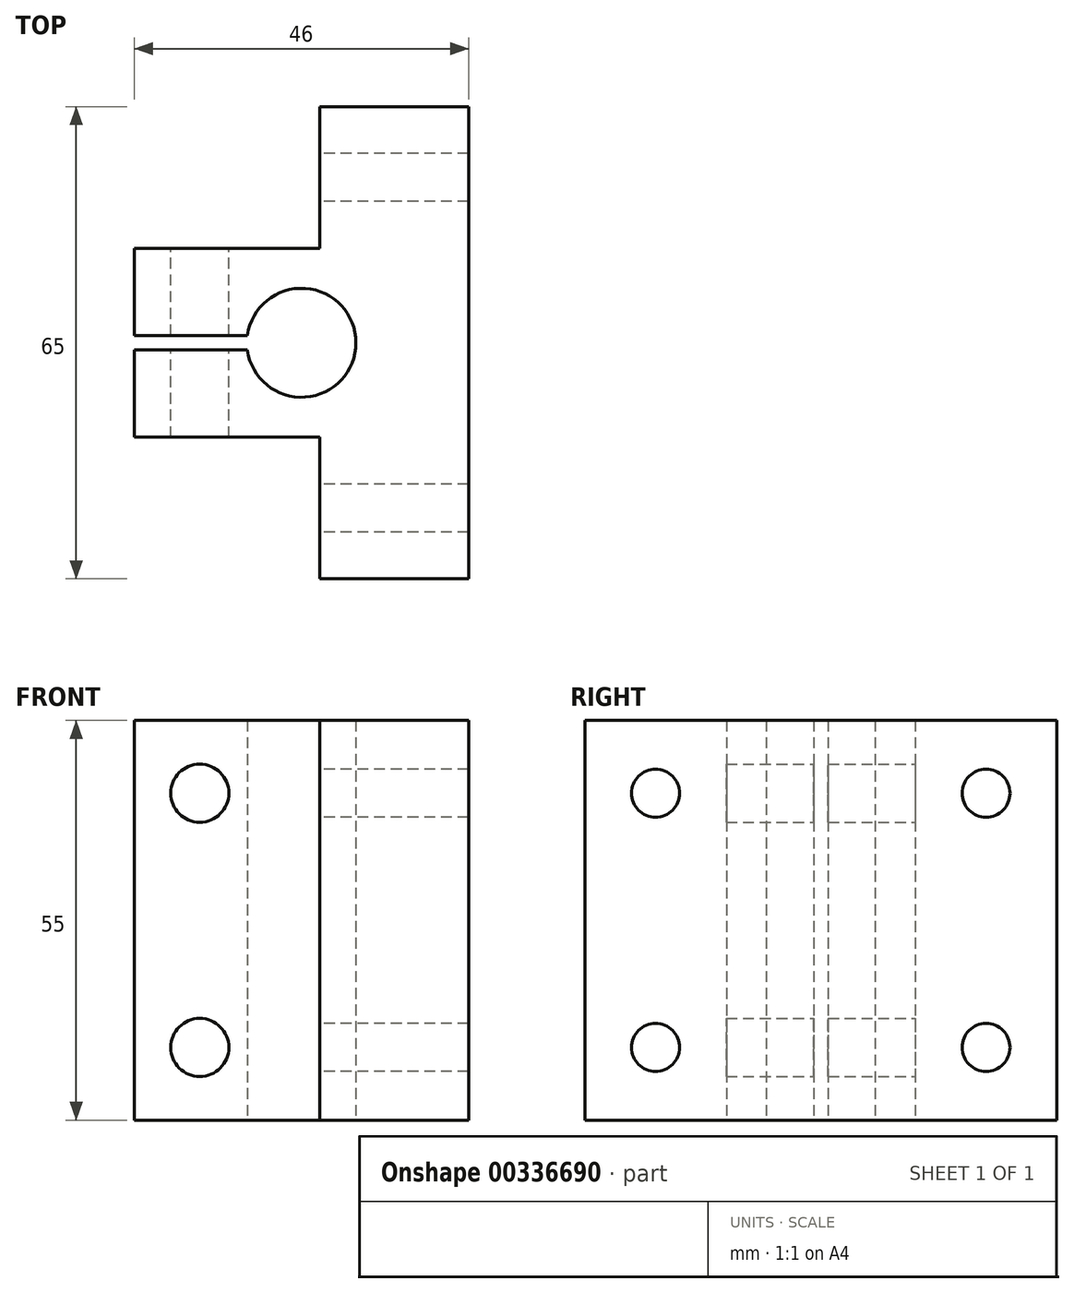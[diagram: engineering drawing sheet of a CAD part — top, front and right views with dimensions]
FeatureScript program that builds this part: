
annotation { "Feature Type Name" : "Feature", "Feature Type Description" : "" }
export const myFeature = defineFeature(function(context is Context, id is Id, definition is map)
    precondition{}
    {
        {
            var Q0;
            Q0=qCreatedBy(makeId("Top.planeOp"),FACE);
            var sketch = newSketch(context, id + "F0", { "sketchPlane" : qUnion([Q0])});
            skLineSegment(sketch, "E0", {"start": v(30.45, -26.3) * mm, "end": v(30.45, 38.7) * mm});
            skLineSegment(sketch, "E1", {"start": v(30.45, 38.7) * mm, "end": v(9.95, 38.7) * mm});
            skLineSegment(sketch, "E2", {"start": v(9.95, 38.7) * mm, "end": v(9.95, 19.2) * mm});
            skLineSegment(sketch, "E3", {"start": v(9.95, 19.2) * mm, "end": v(-15.55, 19.2) * mm});
            skLineSegment(sketch, "E4", {"start": v(30.45, -26.3) * mm, "end": v(9.95, -26.3) * mm});
            skLineSegment(sketch, "E5", {"start": v(9.95, -26.3) * mm, "end": v(9.95, -6.8) * mm});
            skLineSegment(sketch, "E6", {"start": v(9.95, -6.8) * mm, "end": v(-15.55, -6.8) * mm});
            skLineSegment(sketch, "E7", {"start": v(-15.55, -6.8) * mm, "end": v(-15.55, 5.2) * mm});
            skLineSegment(sketch, "E8", {"start": v(-15.55, 19.2) * mm, "end": v(-15.55, 7.2) * mm});
            skLineSegment(sketch, "E9", {"start": v(-15.55, 7.2) * mm, "end": v(0.02, 7.2) * mm});
            skLineSegment(sketch, "E10", {"start": v(-15.55, 5.2) * mm, "end": v(0.02, 5.2) * mm});
            skArc(sketch, "E11", {"start": v(0.02, 5.2) * mm, "mid": v(14.95, 6.2) * mm, "end": v(0.02, 7.2) * mm});
            skPoint(sketch, "E12.orphan", {"position": v(7.45, 5.2) * mm});
            skPoint(sketch, "E13.end.orphan", {"position": v(7.45, 7.2) * mm});
            skSolve(sketch);
        }
        {
            var Q0;
            Q0=makeQuery(id+"F0.imprint","IMPRINT",FACE,{"disambiguationData":[TD([[makeQuery(id+"F0.imprint","IMPRINT",EDGE,{"derivedFrom":sQuery(id+"F0.wireOp",EDGE,"E0")}),1.0]])]});
            extrude(context, id + "F1", {"entities" : qUnion([Q0]), "depth" : 55 * mm});
        }
        {
            var Q0;
            Q0=makeQuery(id+"F1.opExtrude","SWEPT_FACE",FACE,{"disambiguationData":[OSD([sQuery(id+"F0.wireOp",EDGE,"E3")])]});
            var sketch = newSketch(context, id + "F2", { "sketchPlane" : qUnion([Q0])});
            skLineSegment(sketch, "E14", {"start": v(15.55, 55) * mm, "end": v(15.55, 45) * mm});
            skLineSegment(sketch, "E15", {"start": v(15.55, 45) * mm, "end": v(6.55, 45) * mm});
            skLineSegment(sketch, "E16", {"start": v(15.55, 0) * mm, "end": v(15.55, 10) * mm});
            skLineSegment(sketch, "E17", {"start": v(15.55, 10) * mm, "end": v(6.55, 10) * mm});
            skCircle(sketch, "E18", {"center": v(6.55, 10) * mm, "radius": 4 * mm});
            skCircle(sketch, "E19", {"center": v(6.55, 45) * mm, "radius": 4 * mm});
            skSolve(sketch);
        }
        {
            var Q0;
            Q0=makeQuery(id+"F2.imprint","IMPRINT",FACE,{"disambiguationData":[TD([[makeQuery(id+"F2.imprint","IMPRINT",EDGE,{"derivedFrom":sQuery(id+"F2.wireOp",EDGE,"E18")}),1.0]])]});
            var Q1;
            Q1=makeQuery(id+"F2.imprint","IMPRINT",FACE,{"disambiguationData":[TD([[makeQuery(id+"F2.imprint","IMPRINT",EDGE,{"derivedFrom":sQuery(id+"F2.wireOp",EDGE,"E19")}),1.0]])]});
            extrude(context, id + "F3", {"entities" : qUnion([Q0, Q1]), "operationType" : NewBodyOperationType.REMOVE, "oppositeDirection" : true, "depth" : 31.4 * mm});
        }
        {
            var Q0;
            Q0=makeQuery(id+"F1.opExtrude","SWEPT_FACE",FACE,{"disambiguationData":[OSD([sQuery(id+"F0.wireOp",EDGE,"E2")])]});
            var sketch = newSketch(context, id + "F4", { "sketchPlane" : qUnion([Q0])});
            skCircle(sketch, "E20", {"center": v(-28.95, 10) * mm, "radius": 3.3 * mm});
            skCircle(sketch, "E21", {"center": v(-28.95, 45) * mm, "radius": 3.3 * mm});
            skSolve(sketch);
        }
        {
            var Q0;
            Q0=makeQuery(id+"F4.imprint","IMPRINT",FACE,{"disambiguationData":[TD([[makeQuery(id+"F4.imprint","IMPRINT",EDGE,{"derivedFrom":sQuery(id+"F4.wireOp",EDGE,"E20")}),1.0]])]});
            var Q1;
            Q1=makeQuery(id+"F4.imprint","IMPRINT",FACE,{"disambiguationData":[TD([[makeQuery(id+"F4.imprint","IMPRINT",EDGE,{"derivedFrom":sQuery(id+"F4.wireOp",EDGE,"E21")}),1.0]])]});
            extrude(context, id + "F5", {"entities" : qUnion([Q0, Q1]), "operationType" : NewBodyOperationType.REMOVE, "oppositeDirection" : true, "depth" : 25 * mm});
        }
        {
            var Q0;
            Q0=makeQuery(id+"F1.opExtrude","SWEPT_FACE",FACE,{"disambiguationData":[OSD([sQuery(id+"F0.wireOp",EDGE,"E5")])]});
            var sketch = newSketch(context, id + "F6", { "sketchPlane" : qUnion([Q0])});
            skCircle(sketch, "E22", {"center": v(16.55, 45) * mm, "radius": 3.3 * mm});
            skCircle(sketch, "E23", {"center": v(16.55, 10) * mm, "radius": 3.3 * mm});
            skSolve(sketch);
        }
        {
            var Q0;
            Q0=makeQuery(id+"F6.imprint","IMPRINT",FACE,{"disambiguationData":[TD([[makeQuery(id+"F6.imprint","IMPRINT",EDGE,{"derivedFrom":sQuery(id+"F6.wireOp",EDGE,"E23")}),1.0]])]});
            var Q1;
            Q1=makeQuery(id+"F6.imprint","IMPRINT",FACE,{"disambiguationData":[TD([[makeQuery(id+"F6.imprint","IMPRINT",EDGE,{"derivedFrom":sQuery(id+"F6.wireOp",EDGE,"E22")}),1.0]])]});
            extrude(context, id + "F7", {"entities" : qUnion([Q0, Q1]), "operationType" : NewBodyOperationType.REMOVE, "oppositeDirection" : true, "depth" : 25 * mm});
        }
    });
